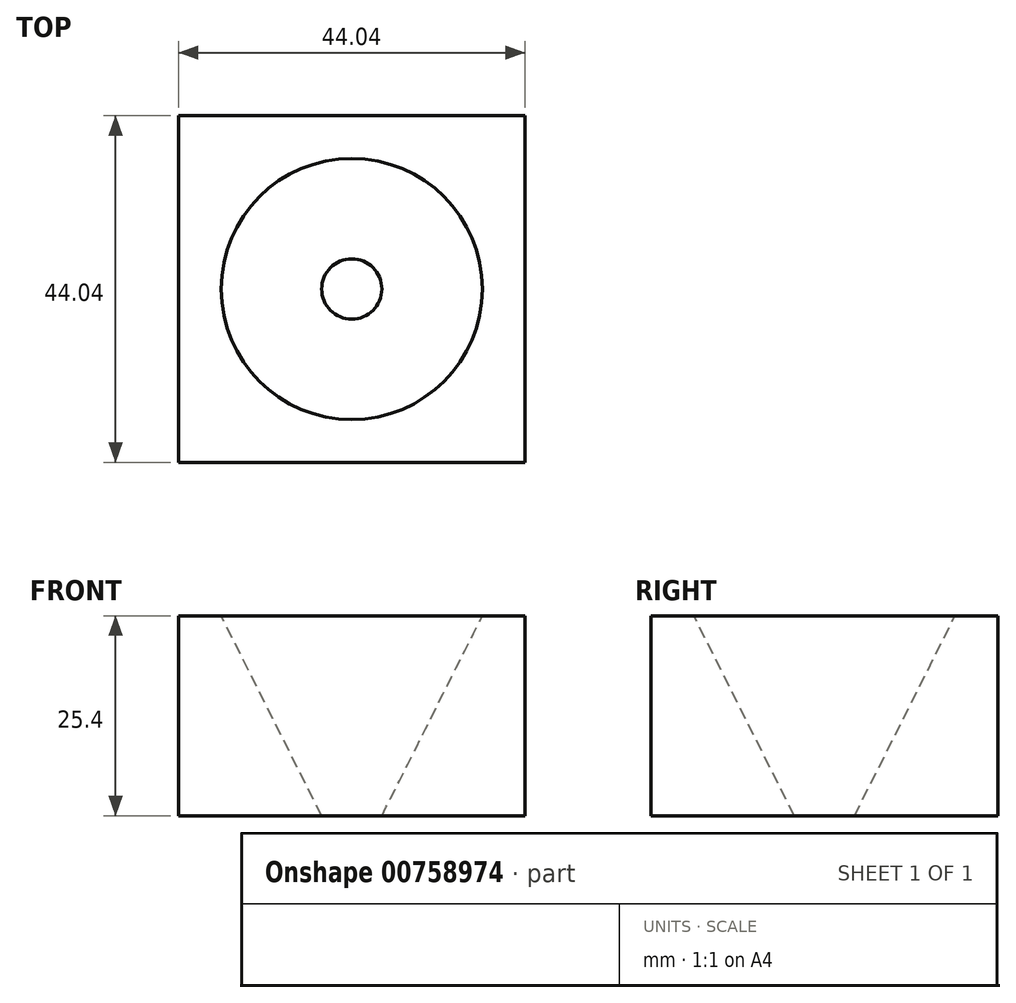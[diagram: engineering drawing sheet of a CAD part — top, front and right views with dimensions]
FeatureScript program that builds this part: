
annotation { "Feature Type Name" : "Feature", "Feature Type Description" : "" }
export const myFeature = defineFeature(function(context is Context, id is Id, definition is map)
    precondition{}
    {
        {
            var Q0;
            Q0=qCreatedBy(makeId("Top.planeOp"),FACE);
            var sketch = newSketch(context, id + "F0", { "sketchPlane" : qUnion([Q0])});
            skLineSegment(sketch, "E0.bottom", {"start": v(22.02, -22.02) * mm, "end": v(-22.02, -22.02) * mm});
            skLineSegment(sketch, "E0.top", {"start": v(22.02, 22.02) * mm, "end": v(-22.02, 22.02) * mm});
            skLineSegment(sketch, "E0.left", {"start": v(22.02, -22.02) * mm, "end": v(22.02, 22.02) * mm});
            skLineSegment(sketch, "E0.right", {"start": v(-22.02, -22.02) * mm, "end": v(-22.02, 22.02) * mm});
            skPoint(sketch, "E0.middle", {"position": v(0, 0) * mm});
            skSolve(sketch);
        }
        {
            var Q0;
            Q0 = qSketchRegion(id + "F0", true);
            extrude(context, id + "F1", {"entities" : qUnion([Q0]), "depth" : 25.4 * mm, "offsetDistance" : 25.4 * mm});
        }
        {
            var Q0;
            Q0=qCreatedBy(makeId("Front.planeOp"),FACE);
            var sketch = newSketch(context, id + "F2", { "sketchPlane" : qUnion([Q0])});
            skLineSegment(sketch, "E1", {"start": v(0, 30.48) * mm, "end": v(19.13, 30.48) * mm});
            skLineSegment(sketch, "E2", {"start": v(19.13, 30.48) * mm, "end": v(0, -7.62) * mm});
            skLineSegment(sketch, "E3", {"start": v(0, -7.62) * mm, "end": v(0, 30.48) * mm});
            skSolve(sketch);
        }
        {
            var Q0;
            Q0 = qSketchRegion(id + "F2", true);
            var Q1;
            Q1=sQuery(id+"F2.wireOp",EDGE,"E3");
            revolve(context, id + "F3", {"surfaceOperationType" : NewSurfaceOperationType.NEW, "entities" : qUnion([Q0]), "axis" : qUnion([Q1]), "revolveType" : RevolveType.FULL});
        }
        {
            var Q0;
            Q0=makeQuery(id+"F3.opRevolve","SWEPT_BODY",BODY,{"disambiguationData":[OSD([sQuery(id+"F2.wireOp",EDGE,"E1"),sQuery(id+"F2.wireOp",EDGE,"E2"),sQuery(id+"F2.wireOp",EDGE,"E3")])]});
            var Q1;
            Q1=makeQuery(id+"F1.opExtrude","SWEPT_BODY",BODY,{"disambiguationData":[OSD([sQuery(id+"F0.wireOp",EDGE,"E0.bottom"),sQuery(id+"F0.wireOp",EDGE,"E0.top"),sQuery(id+"F0.wireOp",EDGE,"E0.left"),sQuery(id+"F0.wireOp",EDGE,"E0.right")])]});
            booleanBodies(context, id + "F4", {"operationType" : BooleanOperationType.SUBTRACTION, "tools" : qUnion([Q0]), "targets" : qUnion([Q1])});
        }
    });
